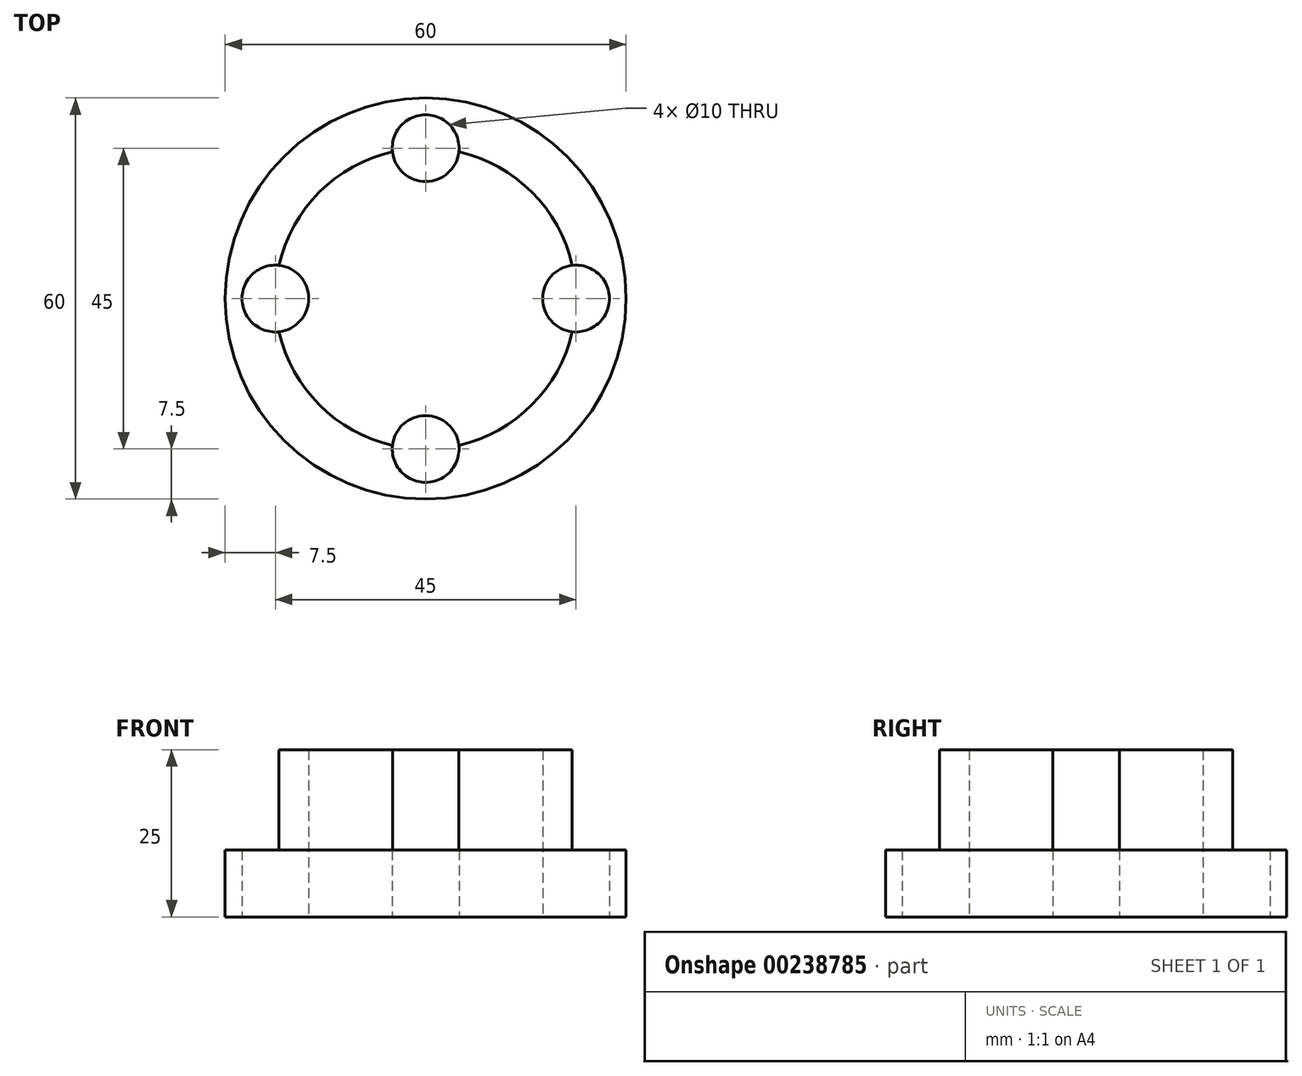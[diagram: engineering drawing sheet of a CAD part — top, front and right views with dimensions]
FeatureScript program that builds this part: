
annotation { "Feature Type Name" : "Feature", "Feature Type Description" : "" }
export const myFeature = defineFeature(function(context is Context, id is Id, definition is map)
    precondition{}
    {
        {
            var Q0;
            Q0=qCreatedBy(makeId("Top.planeOp"),FACE);
            var sketch = newSketch(context, id + "F0", { "sketchPlane" : qUnion([Q0])});
            skCircle(sketch, "E0", {"center": v(0, 0) * mm, "radius": 30 * mm});
            skCircle(sketch, "E1", {"center": v(0, 0) * mm, "radius": 22.5 * mm});
            skLineSegment(sketch, "E2", {"start": v(0, 39.12) * mm, "end": v(0, -37.78) * mm, "construction": true});
            skCircle(sketch, "E3", {"center": v(0, 22.5) * mm, "radius": 5 * mm});
            skCircle(sketch, "E4", {"center": v(0, 22.5) * mm, "radius": 3.5 * mm});
            skCircle(sketch, "E5.1.0", {"center": v(-22.5, 0) * mm, "radius": 3.5 * mm});
            skCircle(sketch, "E5.1.1", {"center": v(-22.5, 0) * mm, "radius": 5 * mm});
            skCircle(sketch, "E5.2.0", {"center": v(0, -22.5) * mm, "radius": 3.5 * mm});
            skCircle(sketch, "E5.2.1", {"center": v(0, -22.5) * mm, "radius": 5 * mm});
            skCircle(sketch, "E5.3.0", {"center": v(22.5, 0) * mm, "radius": 3.5 * mm});
            skCircle(sketch, "E5.3.1", {"center": v(22.5, 0) * mm, "radius": 5 * mm});
            skSolve(sketch);
        }
        {
            var Q0;
            {var subQ1=sQuery(id+"F0.wireOp",EDGE,"E1");var subQ3=sQuery(id+"F0.wireOp",EDGE,"E5.3.1");var subQ12=makeQuery(id+"F0.imprint","INTERSECT",VERTEX,{"disambiguationData":[OD(0.0)],"derivedFrom":[subQ1,subQ3]});Q0=makeQuery(id+"F0.imprint","IMPRINT",FACE,{"disambiguationData":[TD([[makeQuery(id+"F0.imprint","IMPRINT",EDGE,{"disambiguationData":[TD([[subQ12,-1.0]])],"derivedFrom":subQ1}),1.0]])]});}
            extrude(context, id + "F1", {"entities" : qUnion([Q0]), "depth" : 25 * mm});
        }
        {
            var Q0;
            Q0=makeQuery(id+"F0.imprint","IMPRINT",FACE,{"disambiguationData":[TD([[makeQuery(id+"F0.imprint","IMPRINT",EDGE,{"derivedFrom":sQuery(id+"F0.wireOp",EDGE,"E0")}),1.0]])]});
            extrude(context, id + "F2", {"entities" : qUnion([Q0]), "operationType" : NewBodyOperationType.ADD, "depth" : 10 * mm});
        }
    });
